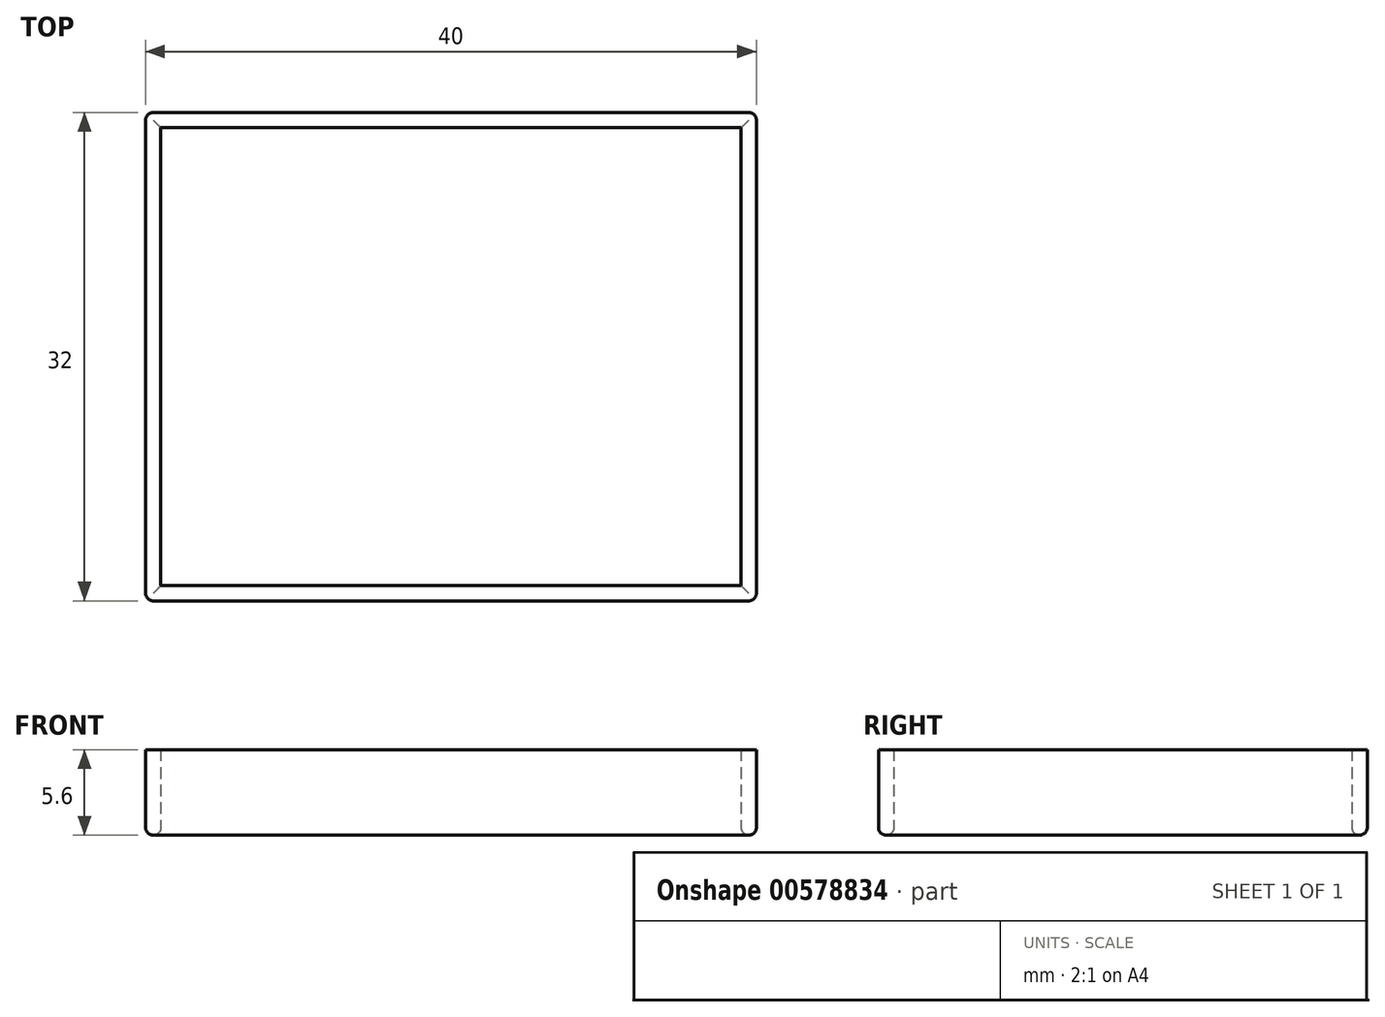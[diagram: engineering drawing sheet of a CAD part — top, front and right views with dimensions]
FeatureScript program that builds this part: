
annotation { "Feature Type Name" : "Feature", "Feature Type Description" : "" }
export const myFeature = defineFeature(function(context is Context, id is Id, definition is map)
    precondition{}
    {
        {
            var Q0;
            Q0=qCreatedBy(makeId("Top.planeOp"),FACE);
            var sketch = newSketch(context, id + "F0", { "sketchPlane" : qUnion([Q0])});
            skLineSegment(sketch, "E0.bottom", {"start": v(-20, 16) * mm, "end": v(20, 16) * mm});
            skLineSegment(sketch, "E0.top", {"start": v(-20, -16) * mm, "end": v(20, -16) * mm});
            skLineSegment(sketch, "E0.left", {"start": v(-20, 16) * mm, "end": v(-20, -16) * mm});
            skLineSegment(sketch, "E0.right", {"start": v(20, 16) * mm, "end": v(20, -16) * mm});
            skPoint(sketch, "E0.middle", {"position": v(0, 0) * mm});
            skLineSegment(sketch, "E1.0", {"start": v(19, 15) * mm, "end": v(19, -15) * mm});
            skLineSegment(sketch, "E1.1", {"start": v(-19, 15) * mm, "end": v(19, 15) * mm});
            skLineSegment(sketch, "E1.2", {"start": v(-19, 15) * mm, "end": v(-19, -15) * mm});
            skLineSegment(sketch, "E1.3", {"start": v(-19, -15) * mm, "end": v(19, -15) * mm});
            skSolve(sketch);
        }
        {
            var Q0;
            Q0 = qSketchRegion(id + "F0", true);
            extrude(context, id + "F1", {"entities" : qUnion([Q0]), "depth" : 5.6 * mm, "offsetDistance" : 25 * mm});
        }
        {
            var Q0;
            Q0=makeQuery(id+"F1.opExtrude","CAP_FACE",FACE,{"disambiguationData":[OSD([sQuery(id+"F0.wireOp",EDGE,"E0.bottom"),sQuery(id+"F0.wireOp",EDGE,"E0.top"),sQuery(id+"F0.wireOp",EDGE,"E0.left"),sQuery(id+"F0.wireOp",EDGE,"E0.right"),sQuery(id+"F0.wireOp",EDGE,"E1.0"),sQuery(id+"F0.wireOp",EDGE,"E1.1"),sQuery(id+"F0.wireOp",EDGE,"E1.2"),sQuery(id+"F0.wireOp",EDGE,"E1.3")])],"isStart":true});
            var Q1;
            Q1=makeQuery(id+"F1.opExtrude","SWEPT_EDGE",EDGE,{"disambiguationData":[OSD([sQuery(id+"F0.wireOp",EDGE,"E0.top"),sQuery(id+"F0.wireOp",EDGE,"E0.left")])]});
            var Q2;
            Q2=makeQuery(id+"F1.opExtrude","SWEPT_EDGE",EDGE,{"disambiguationData":[OSD([sQuery(id+"F0.wireOp",EDGE,"E0.top"),sQuery(id+"F0.wireOp",EDGE,"E0.right")])]});
            var Q3;
            Q3=makeQuery(id+"F1.opExtrude","SWEPT_EDGE",EDGE,{"disambiguationData":[OSD([sQuery(id+"F0.wireOp",EDGE,"E0.bottom"),sQuery(id+"F0.wireOp",EDGE,"E0.left")])]});
            var Q4;
            Q4=makeQuery(id+"F1.opExtrude","SWEPT_EDGE",EDGE,{"disambiguationData":[OSD([sQuery(id+"F0.wireOp",EDGE,"E0.bottom"),sQuery(id+"F0.wireOp",EDGE,"E0.right")])]});
            fillet(context, id + "F2", {"entities" : qUnion([Q0, Q1, Q2, Q3, Q4]), "radius" : 0.5 * mm, "tangentPropagation" : true, "allowEdgeOverflow" : false});
        }
    });
